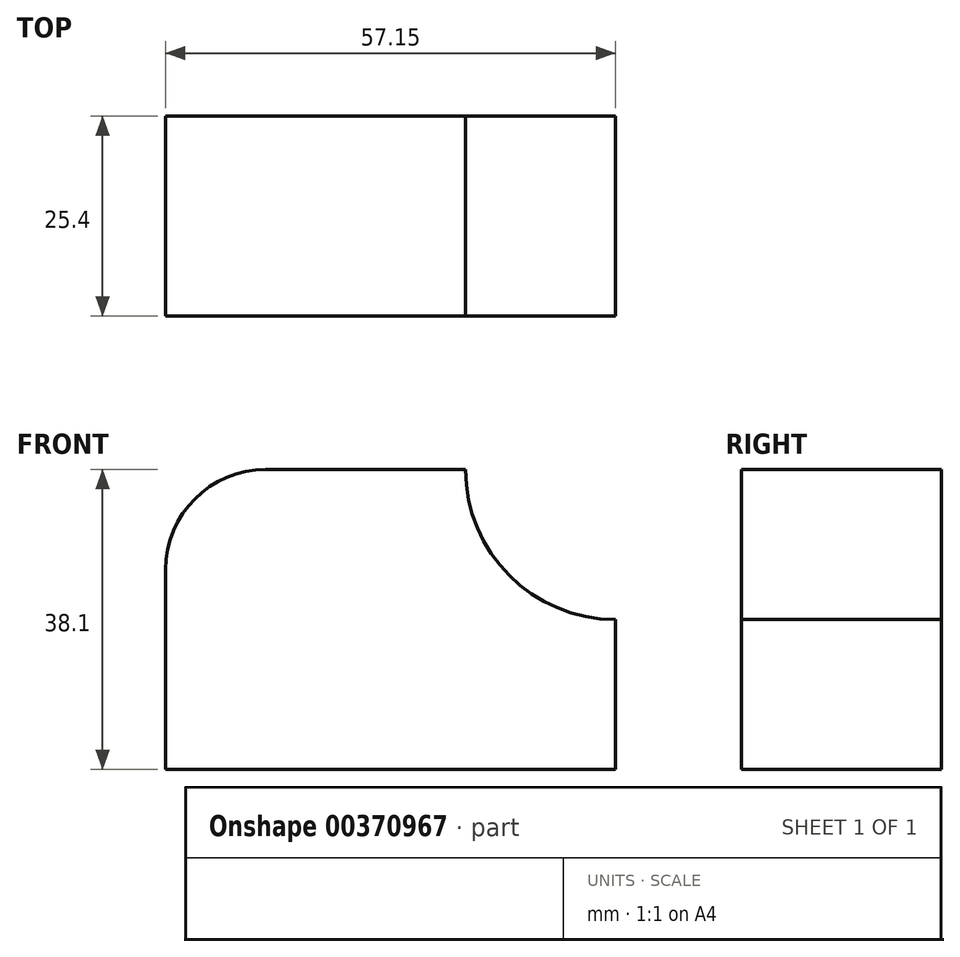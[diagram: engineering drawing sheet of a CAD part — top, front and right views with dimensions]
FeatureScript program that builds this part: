
annotation { "Feature Type Name" : "Feature", "Feature Type Description" : "" }
export const myFeature = defineFeature(function(context is Context, id is Id, definition is map)
    precondition{}
    {
        {
            var Q0;
            Q0=qCreatedBy(makeId("Front.planeOp"),FACE);
            var sketch = newSketch(context, id + "F0", { "sketchPlane" : qUnion([Q0])});
            skLineSegment(sketch, "E0", {"start": v(0, 0) * mm, "end": v(57.15, 0) * mm});
            skLineSegment(sketch, "E1", {"start": v(57.15, 0) * mm, "end": v(57.15, 19.05) * mm});
            skLineSegment(sketch, "E2", {"start": v(0, 0) * mm, "end": v(0, 38.1) * mm});
            skLineSegment(sketch, "E3", {"start": v(0, 38.1) * mm, "end": v(38.1, 38.1) * mm});
            skArc(sketch, "E4", {"start": v(38.1, 38.1) * mm, "mid": v(43.68, 24.63) * mm, "end": v(57.15, 19.05) * mm});
            skSolve(sketch);
        }
        {
            var Q0;
            Q0=makeQuery(id+"F0.imprint","IMPRINT",FACE,{"disambiguationData":[TD([[makeQuery(id+"F0.imprint","IMPRINT",EDGE,{"derivedFrom":sQuery(id+"F0.wireOp",EDGE,"E0")}),1.0]])]});
            extrude(context, id + "F1", {"entities" : qUnion([Q0]), "oppositeDirection" : true, "depth" : 25.4 * mm});
        }
        {
            var Q0;
            Q0=makeQuery(id+"F1.opExtrude","SWEPT_EDGE",EDGE,{"disambiguationData":[OSD([sQuery(id+"F0.wireOp",EDGE,"E2"),sQuery(id+"F0.wireOp",EDGE,"E3")])]});
            fillet(context, id + "F2", {"entities" : qUnion([Q0]), "radius" : 12.7 * mm, "tangentPropagation" : true, "allowEdgeOverflow" : false});
        }
    });
